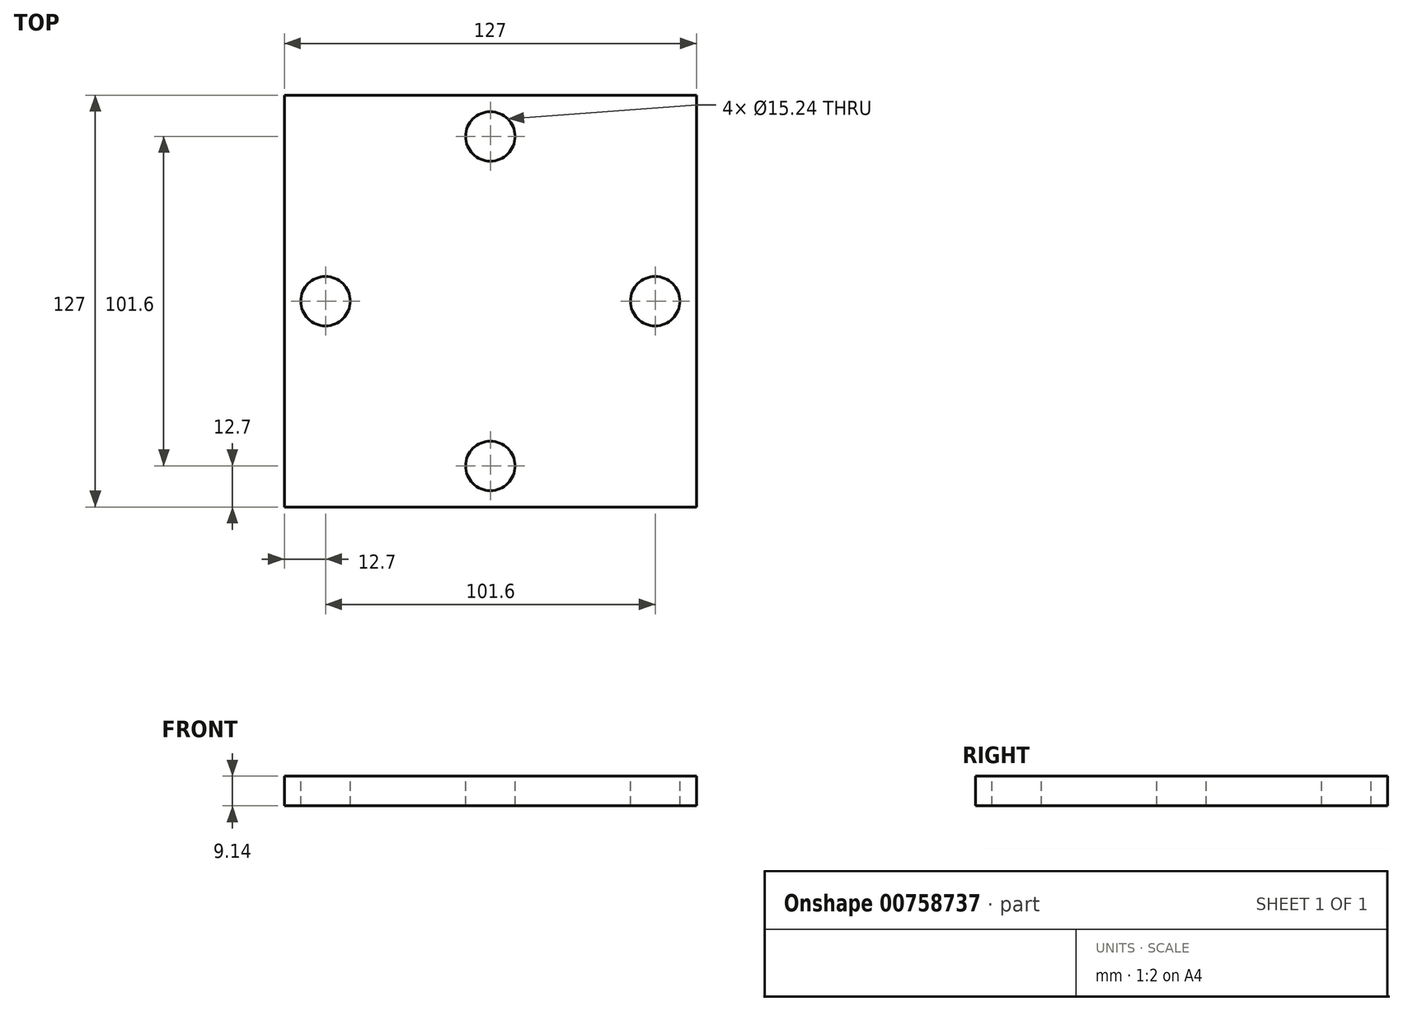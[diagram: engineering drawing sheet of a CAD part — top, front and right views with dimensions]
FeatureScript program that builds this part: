
annotation { "Feature Type Name" : "Feature", "Feature Type Description" : "" }
export const myFeature = defineFeature(function(context is Context, id is Id, definition is map)
    precondition{}
    {
        {
            var Q0;
            Q0=qCreatedBy(makeId("Top.planeOp"),FACE);
            var sketch = newSketch(context, id + "F0", { "sketchPlane" : qUnion([Q0])});
            skLineSegment(sketch, "E0.bottom", {"start": v(0, 0) * mm, "end": v(127, 0) * mm});
            skLineSegment(sketch, "E0.top", {"start": v(0, -127) * mm, "end": v(127, -127) * mm});
            skLineSegment(sketch, "E0.left", {"start": v(0, 0) * mm, "end": v(0, -127) * mm});
            skLineSegment(sketch, "E0.right", {"start": v(127, 0) * mm, "end": v(127, -127) * mm});
            skSolve(sketch);
        }
        {
            var Q0;
            Q0=makeQuery(id+"F0.imprint","IMPRINT",FACE,{"disambiguationData":[TD([[makeQuery(id+"F0.imprint","IMPRINT",EDGE,{"derivedFrom":sQuery(id+"F0.wireOp",EDGE,"E0.bottom")}),-1.0]])]});
            extrude(context, id + "F1", {"entities" : qUnion([Q0]), "depth" : 9.14 * mm, "offsetDistance" : 25.4 * mm});
        }
        {
            var Q0;
            Q0=makeQuery(id+"F1.opExtrude","CAP_FACE",FACE,{"disambiguationData":[OSD([sQuery(id+"F0.wireOp",EDGE,"E0.bottom"),sQuery(id+"F0.wireOp",EDGE,"E0.top"),sQuery(id+"F0.wireOp",EDGE,"E0.left"),sQuery(id+"F0.wireOp",EDGE,"E0.right")])],"isStart":false});
            var sketch = newSketch(context, id + "F2", { "sketchPlane" : qUnion([Q0])});
            skLineSegment(sketch, "E1", {"start": v(63.5, 0) * mm, "end": v(63.5, -12.7) * mm});
            skCircle(sketch, "E2", {"center": v(63.5, -12.7) * mm, "radius": 6.35 * mm});
            skLineSegment(sketch, "E3", {"start": v(0, -63.5) * mm, "end": v(12.7, -63.5) * mm});
            skCircle(sketch, "E4", {"center": v(12.7, -63.5) * mm, "radius": 6.35 * mm});
            skLineSegment(sketch, "E5", {"start": v(63.5, -127) * mm, "end": v(63.5, -114.3) * mm});
            skCircle(sketch, "E6", {"center": v(63.5, -114.3) * mm, "radius": 6.35 * mm});
            skLineSegment(sketch, "E7", {"start": v(127, -63.5) * mm, "end": v(114.3, -63.5) * mm});
            skCircle(sketch, "E8", {"center": v(114.3, -63.5) * mm, "radius": 6.35 * mm});
            skSolve(sketch);
        }
        {
            var Q0;
            Q0=sQuery(id+"F2.wireOp",VERTEX,"E1.end");
            var Q1;
            Q1=makeQuery(id+"F1.opExtrude","SWEPT_BODY",BODY,{"disambiguationData":[OSD([sQuery(id+"F0.wireOp",EDGE,"E0.bottom"),sQuery(id+"F0.wireOp",EDGE,"E0.top"),sQuery(id+"F0.wireOp",EDGE,"E0.left"),sQuery(id+"F0.wireOp",EDGE,"E0.right")])]});
            hole(context, id + "F3", {"style" : HoleStyle.C_BORE, "endStyle" : HoleEndStyle.THROUGH, "holeDiameter" : 15.24 * mm, "cBoreDiameter" : 15.24 * mm, "cBoreDepth" : 50.8 * mm, "majorDiameter" : 6.35 * mm, "isTappedThrough" : true, "tappedDepth" : 12.7 * mm, "tapClearance" : 3, "locations" : qUnion([Q0]), "scope" : qUnion([Q1])});
        }
        {
            var Q0;
            Q0=sQuery(id+"F2.wireOp",VERTEX,"E3.end");
            var Q1;
            Q1=makeQuery(id+"F1.opExtrude","SWEPT_BODY",BODY,{"disambiguationData":[OSD([sQuery(id+"F0.wireOp",EDGE,"E0.bottom"),sQuery(id+"F0.wireOp",EDGE,"E0.top"),sQuery(id+"F0.wireOp",EDGE,"E0.left"),sQuery(id+"F0.wireOp",EDGE,"E0.right")])]});
            hole(context, id + "F4", {"style" : HoleStyle.C_BORE, "endStyle" : HoleEndStyle.THROUGH, "holeDiameter" : 15.24 * mm, "cBoreDiameter" : 15.24 * mm, "cBoreDepth" : 50.8 * mm, "majorDiameter" : 6.35 * mm, "isTappedThrough" : true, "tappedDepth" : 12.7 * mm, "tapClearance" : 3, "locations" : qUnion([Q0]), "scope" : qUnion([Q1])});
        }
        {
            var Q0;
            Q0=sQuery(id+"F2.wireOp",VERTEX,"E5.end");
            var Q1;
            Q1=makeQuery(id+"F1.opExtrude","SWEPT_BODY",BODY,{"disambiguationData":[OSD([sQuery(id+"F0.wireOp",EDGE,"E0.bottom"),sQuery(id+"F0.wireOp",EDGE,"E0.top"),sQuery(id+"F0.wireOp",EDGE,"E0.left"),sQuery(id+"F0.wireOp",EDGE,"E0.right")])]});
            hole(context, id + "F5", {"style" : HoleStyle.C_BORE, "endStyle" : HoleEndStyle.THROUGH, "holeDiameter" : 15.24 * mm, "cBoreDiameter" : 15.24 * mm, "cBoreDepth" : 50.8 * mm, "majorDiameter" : 6.35 * mm, "isTappedThrough" : true, "tappedDepth" : 12.7 * mm, "tapClearance" : 3, "locations" : qUnion([Q0]), "scope" : qUnion([Q1])});
        }
        {
            var Q0;
            Q0=sQuery(id+"F2.wireOp",VERTEX,"E8.center");
            var Q1;
            Q1=makeQuery(id+"F1.opExtrude","SWEPT_BODY",BODY,{"disambiguationData":[OSD([sQuery(id+"F0.wireOp",EDGE,"E0.bottom"),sQuery(id+"F0.wireOp",EDGE,"E0.top"),sQuery(id+"F0.wireOp",EDGE,"E0.left"),sQuery(id+"F0.wireOp",EDGE,"E0.right")])]});
            hole(context, id + "F6", {"style" : HoleStyle.C_BORE, "endStyle" : HoleEndStyle.THROUGH, "holeDiameter" : 15.24 * mm, "cBoreDiameter" : 15.24 * mm, "cBoreDepth" : 50.8 * mm, "majorDiameter" : 6.35 * mm, "isTappedThrough" : true, "tappedDepth" : 12.7 * mm, "tapClearance" : 3, "locations" : qUnion([Q0]), "scope" : qUnion([Q1])});
        }
    });
